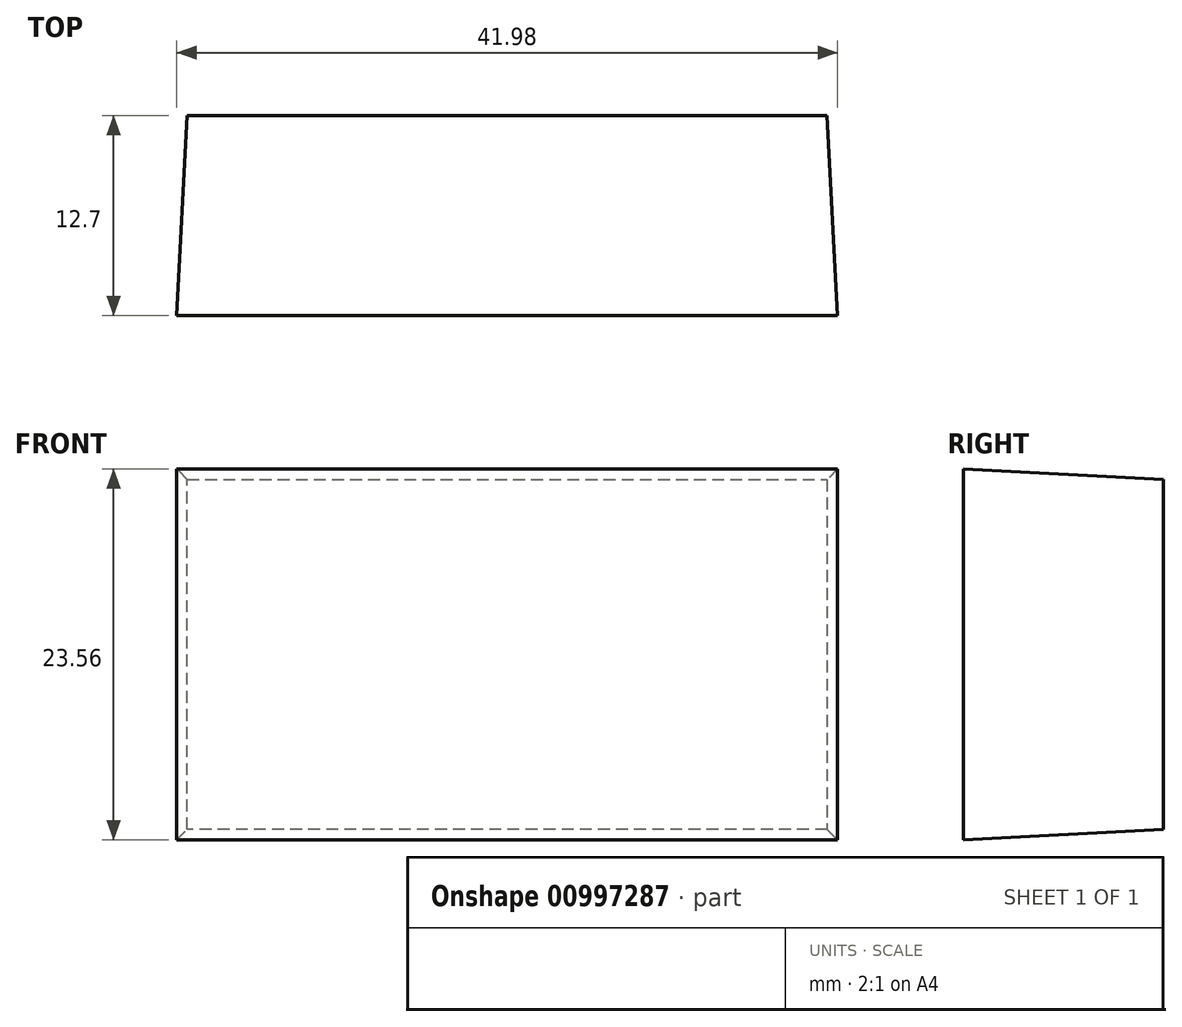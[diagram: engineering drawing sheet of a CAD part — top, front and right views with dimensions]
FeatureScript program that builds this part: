
annotation { "Feature Type Name" : "Feature", "Feature Type Description" : "" }
export const myFeature = defineFeature(function(context is Context, id is Id, definition is map)
    precondition{}
    {
        {
            var Q0;
            Q0=qCreatedBy(makeId("Front.planeOp"),FACE);
            var sketch = newSketch(context, id + "F0", { "sketchPlane" : qUnion([Q0])});
            skLineSegment(sketch, "E0.bottom", {"start": v(20.32, -11.11) * mm, "end": v(-20.32, -11.11) * mm});
            skLineSegment(sketch, "E0.top", {"start": v(20.32, 11.11) * mm, "end": v(-20.32, 11.11) * mm});
            skLineSegment(sketch, "E0.left", {"start": v(20.32, -11.11) * mm, "end": v(20.32, 11.11) * mm});
            skLineSegment(sketch, "E0.right", {"start": v(-20.32, -11.11) * mm, "end": v(-20.32, 11.11) * mm});
            skPoint(sketch, "E0.middle", {"position": v(0, 0) * mm});
            skSolve(sketch);
        }
        {
            var Q0;
            Q0 = qSketchRegion(id + "F0", true);
            extrude(context, id + "F1", {"entities" : qUnion([Q0]), "depth" : 12.7 * mm, "offsetDistance" : 25.4 * mm, "hasDraft" : true, "draftAngle" : 3 * degree});
        }
    });
